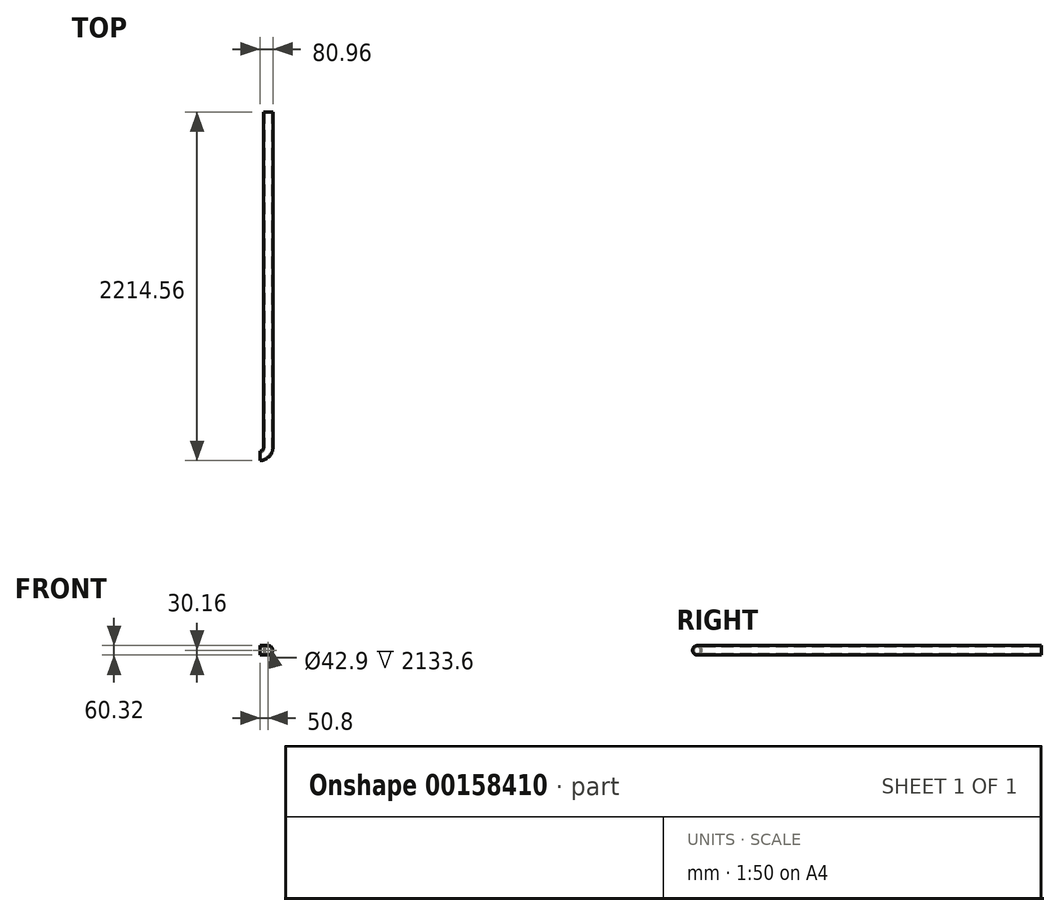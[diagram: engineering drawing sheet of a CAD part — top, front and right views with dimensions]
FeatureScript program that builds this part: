
annotation { "Feature Type Name" : "Feature", "Feature Type Description" : "" }
export const myFeature = defineFeature(function(context is Context, id is Id, definition is map)
    precondition{}
    {
        {
            var Q0;
            Q0=qCreatedBy(makeId("Front.planeOp"),FACE);
            var sketch = newSketch(context, id + "F0", { "sketchPlane" : qUnion([Q0])});
            skCircle(sketch, "E0", {"center": v(0, 0) * mm, "radius": 30.16 * mm});
            skCircle(sketch, "E1.0", {"center": v(0, 0) * mm, "radius": 21.45 * mm});
            skSolve(sketch);
        }
        {
            var Q0;
            Q0=qCreatedBy(makeId("Top.planeOp"),FACE);
            var sketch = newSketch(context, id + "F1", { "sketchPlane" : qUnion([Q0])});
            skLineSegment(sketch, "E2", {"start": v(0, 0) * mm, "end": v(0, -2133.6) * mm});
            skLineSegment(sketch, "E3", {"start": v(0, -2133.6) * mm, "end": v(-50.8, -2133.6) * mm, "construction": true});
            skArc(sketch, "E4", {"start": v(0, -2133.6) * mm, "mid": v(-14.88, -2169.52) * mm, "end": v(-50.8, -2184.4) * mm});
            skSolve(sketch);
        }
        {
            var Q0;
            Q0=makeQuery(id+"F0.imprint","IMPRINT",FACE,{"disambiguationData":[TD([[makeQuery(id+"F0.imprint","IMPRINT",EDGE,{"derivedFrom":sQuery(id+"F0.wireOp",EDGE,"E0")}),1.0]])]});
            var Q1;
            Q1=sQuery(id+"F1.wireOp",EDGE,"E2");
            var Q2;
            Q2=sQuery(id+"F1.wireOp",EDGE,"E4");
            sweep(context, id + "F2", {"profiles" : qUnion([Q0]), "path" : qUnion([Q1, Q2])});
        }
    });
